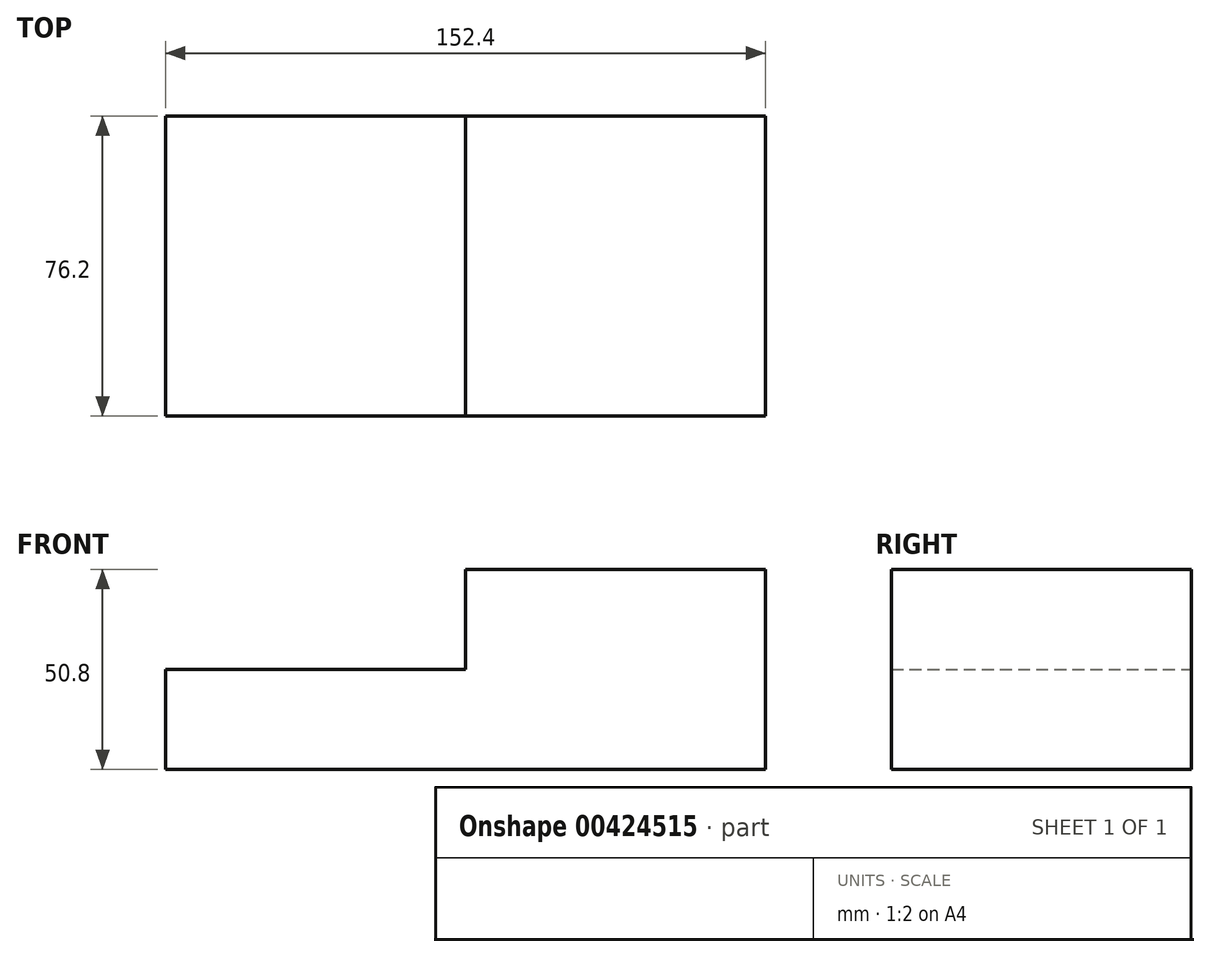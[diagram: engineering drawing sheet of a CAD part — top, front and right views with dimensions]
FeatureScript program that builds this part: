
annotation { "Feature Type Name" : "Feature", "Feature Type Description" : "" }
export const myFeature = defineFeature(function(context is Context, id is Id, definition is map)
    precondition{}
    {
        {
            var Q0;
            Q0=qCreatedBy(makeId("Front.planeOp"),FACE);
            var sketch = newSketch(context, id + "F0", { "sketchPlane" : qUnion([Q0])});
            skLineSegment(sketch, "E0", {"start": v(0, 0) * mm, "end": v(0, 25.4) * mm});
            skLineSegment(sketch, "E1", {"start": v(0, 25.4) * mm, "end": v(76.2, 25.4) * mm});
            skLineSegment(sketch, "E2", {"start": v(0, 0) * mm, "end": v(152.4, 0) * mm});
            skLineSegment(sketch, "E3", {"start": v(76.2, 25.4) * mm, "end": v(76.2, 50.8) * mm});
            skLineSegment(sketch, "E4", {"start": v(76.2, 50.8) * mm, "end": v(152.4, 50.8) * mm});
            skLineSegment(sketch, "E5", {"start": v(152.4, 50.8) * mm, "end": v(152.4, 0) * mm});
            skSolve(sketch);
        }
        {
            var Q0;
            Q0=makeQuery(id+"F0.imprint","IMPRINT",FACE,{"disambiguationData":[TD([[makeQuery(id+"F0.imprint","IMPRINT",EDGE,{"derivedFrom":sQuery(id+"F0.wireOp",EDGE,"E0")}),-1.0]])]});
            extrude(context, id + "F1", {"entities" : qUnion([Q0]), "depth" : 76.2 * mm});
        }
    });
